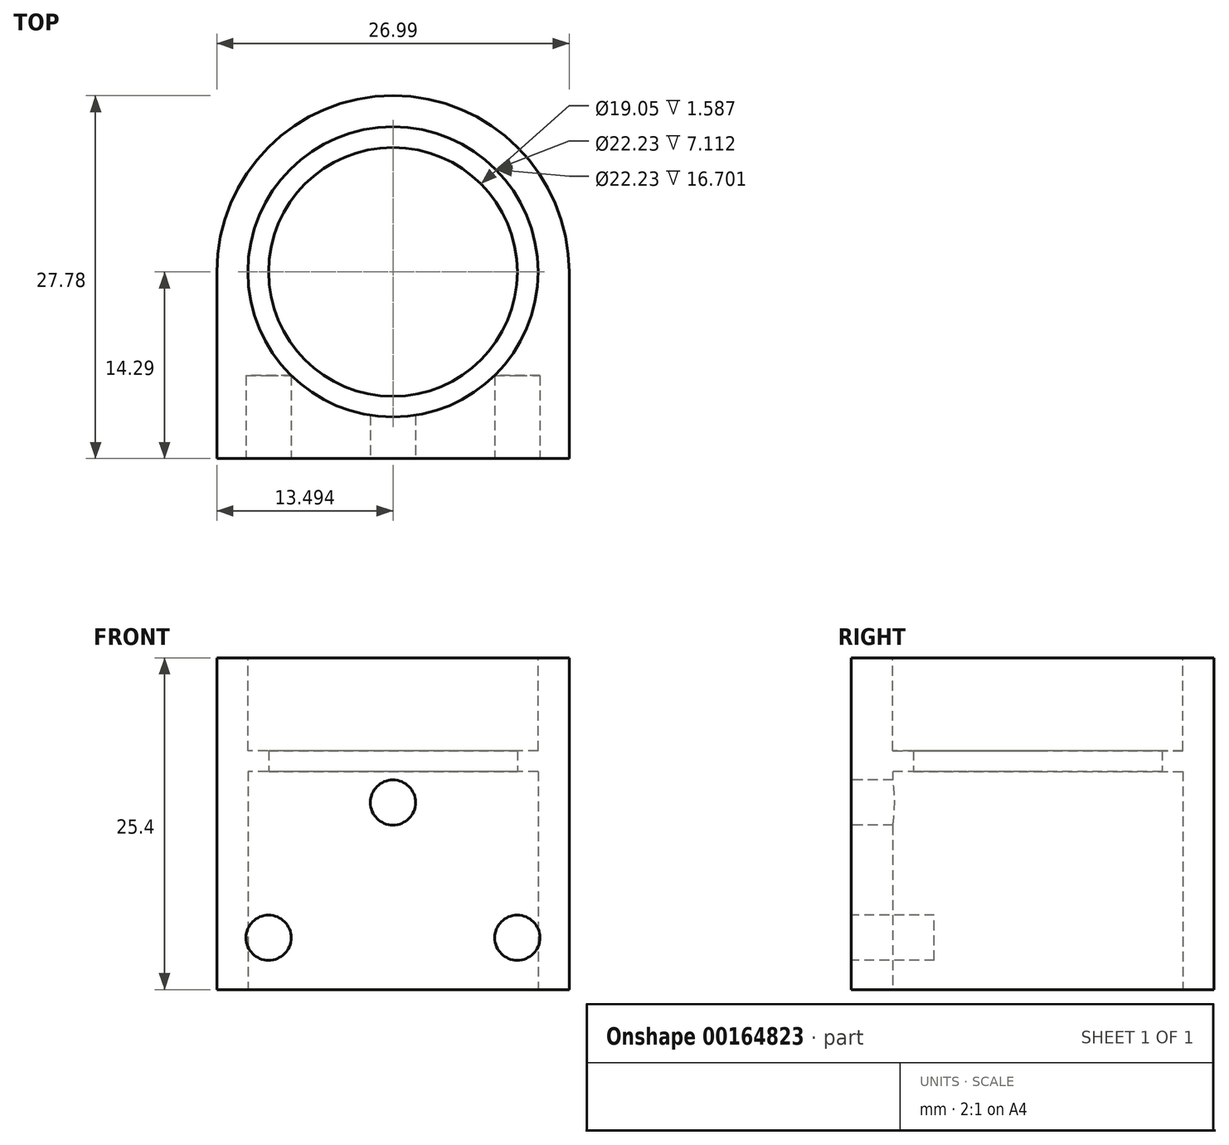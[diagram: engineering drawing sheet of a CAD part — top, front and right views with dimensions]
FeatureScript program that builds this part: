
annotation { "Feature Type Name" : "Feature", "Feature Type Description" : "" }
export const myFeature = defineFeature(function(context is Context, id is Id, definition is map)
    precondition{}
    {
        {
            var Q0;
            Q0=qCreatedBy(makeId("Top.planeOp"),FACE);
            var sketch = newSketch(context, id + "F0", { "sketchPlane" : qUnion([Q0])});
            skLineSegment(sketch, "E0.bottom", {"start": v(0, 0) * mm, "end": v(26.99, 0) * mm, "construction": true});
            skLineSegment(sketch, "E0.top", {"start": v(0, -14.29) * mm, "end": v(26.99, -14.29) * mm});
            skLineSegment(sketch, "E0.left", {"start": v(0, 0) * mm, "end": v(0, -14.29) * mm});
            skLineSegment(sketch, "E0.right", {"start": v(26.99, 0) * mm, "end": v(26.99, -14.29) * mm});
            skArc(sketch, "E1", {"start": v(26.99, 0) * mm, "mid": v(13.5, 13.5) * mm, "end": v(0, 0) * mm});
            skCircle(sketch, "E2", {"center": v(13.5, 0) * mm, "radius": 9.53 * mm});
            skArc(sketch, "E3", {"start": v(0, 0) * mm, "mid": v(13.5, -13.5) * mm, "end": v(26.99, 0) * mm, "construction": true});
            skLineSegment(sketch, "E4", {"start": v(23.02, -14.29) * mm, "end": v(23.02, -9.52) * mm, "construction": true});
            skLineSegment(sketch, "E5", {"start": v(19.05, -9.52) * mm, "end": v(26.99, -9.52) * mm, "construction": true});
            skSolve(sketch);
        }
        {
            var Q0;
            Q0 = qSketchRegion(id + "F0", true);
            extrude(context, id + "F1", {"entities" : qUnion([Q0]), "depth" : 25.4 * mm});
        }
        {
            var Q0;
            Q0=makeQuery(id+"F1.opExtrude","CAP_FACE",FACE,{"disambiguationData":[OSD([sQuery(id+"F0.wireOp",EDGE,"E0.top"),sQuery(id+"F0.wireOp",EDGE,"E0.left"),sQuery(id+"F0.wireOp",EDGE,"E0.right"),sQuery(id+"F0.wireOp",EDGE,"E1"),sQuery(id+"F0.wireOp",EDGE,"E2")])],"isStart":false});
            var sketch = newSketch(context, id + "F2", { "sketchPlane" : qUnion([Q0])});
            skCircle(sketch, "E6", {"center": v(13.5, 0) * mm, "radius": 11.11 * mm});
            skSolve(sketch);
        }
        {
            var Q0;
            Q0 = qSketchRegion(id + "F2", true);
            extrude(context, id + "F3", {"entities" : qUnion([Q0]), "operationType" : NewBodyOperationType.REMOVE, "oppositeDirection" : true, "depth" : 7.11 * mm});
        }
        {
            var Q0;
            Q0=makeQuery(id+"F3.boolean.opBoolean","COPY",FACE,{"derivedFrom":makeQuery(id+"F3.opExtrude","CAP_FACE",FACE,{"disambiguationData":[OSD([sQuery(id+"F2.wireOp",EDGE,"E6")])],"isStart":false})});
            cPlane(context, id + "F4", {"entities" : qUnion([Q0]), "cplaneType" : CPlaneType.OFFSET, "offset" : 1.59 * mm, "oppositeDirection" : true, "width" : 152.4 * mm, "height" : 152.4 * mm});
        }
        {
            var Q0;
            Q0=makeQuery(id+"F1.opExtrude","CAP_FACE",FACE,{"disambiguationData":[OSD([sQuery(id+"F0.wireOp",EDGE,"E0.top"),sQuery(id+"F0.wireOp",EDGE,"E0.left"),sQuery(id+"F0.wireOp",EDGE,"E0.right"),sQuery(id+"F0.wireOp",EDGE,"E1"),sQuery(id+"F0.wireOp",EDGE,"E2")])],"isStart":true});
            var sketch = newSketch(context, id + "F5", { "sketchPlane" : qUnion([Q0])});
            skCircle(sketch, "E7", {"center": v(13.5, 0) * mm, "radius": 11.11 * mm});
            skSolve(sketch);
        }
        {
            var Q0;
            Q0 = qSketchRegion(id + "F5", true);
            var Q1;
            Q1=qCreatedBy(id+"F4.planeOp",FACE);
            extrude(context, id + "F6", {"entities" : qUnion([Q0]), "operationType" : NewBodyOperationType.REMOVE, "endBound" : BoundingType.UP_TO_SURFACE, "oppositeDirection" : true, "endBoundEntityFace" : qUnion([Q1]), "depth" : 25.4 * mm});
        }
        {
            var Q0;
            Q0=makeQuery(id+"F1.opExtrude","SWEPT_FACE",FACE,{"disambiguationData":[OSD([sQuery(id+"F0.wireOp",EDGE,"E0.top")])]});
            var sketch = newSketch(context, id + "F7", { "sketchPlane" : qUnion([Q0])});
            skLineSegment(sketch, "E8.bottom", {"start": v(26.99, 0) * mm, "end": v(23.02, 0) * mm, "construction": true});
            skLineSegment(sketch, "E8.top", {"start": v(26.99, 3.97) * mm, "end": v(23.02, 3.97) * mm, "construction": true});
            skLineSegment(sketch, "E8.left", {"start": v(26.99, 0) * mm, "end": v(26.99, 3.97) * mm, "construction": true});
            skLineSegment(sketch, "E8.right", {"start": v(23.02, 0) * mm, "end": v(23.02, 3.97) * mm, "construction": true});
            skLineSegment(sketch, "E9.bottom", {"start": v(0, 0) * mm, "end": v(3.97, 0) * mm, "construction": true});
            skLineSegment(sketch, "E9.top", {"start": v(0, 3.97) * mm, "end": v(3.97, 3.97) * mm, "construction": true});
            skLineSegment(sketch, "E9.left", {"start": v(0, 0) * mm, "end": v(0, 3.97) * mm, "construction": true});
            skLineSegment(sketch, "E9.right", {"start": v(3.97, 0) * mm, "end": v(3.97, 3.97) * mm, "construction": true});
            skCircle(sketch, "E10", {"center": v(23.02, 3.97) * mm, "radius": 1.73 * mm});
            skCircle(sketch, "E11", {"center": v(3.97, 3.97) * mm, "radius": 1.73 * mm});
            skLineSegment(sketch, "E12", {"start": v(13.5, 18.29) * mm, "end": v(13.5, 14.32) * mm, "construction": true});
            skCircle(sketch, "E13", {"center": v(13.5, 14.32) * mm, "radius": 1.73 * mm});
            skSolve(sketch);
        }
        {
            var Q0;
            Q0=makeQuery(id+"F7.imprint","IMPRINT",FACE,{"disambiguationData":[TD([[makeQuery(id+"F7.imprint","IMPRINT",EDGE,{"derivedFrom":sQuery(id+"F7.wireOp",EDGE,"E10")}),1.0]])]});
            var Q1;
            Q1=makeQuery(id+"F7.imprint","IMPRINT",FACE,{"disambiguationData":[TD([[makeQuery(id+"F7.imprint","IMPRINT",EDGE,{"derivedFrom":sQuery(id+"F7.wireOp",EDGE,"E11")}),1.0]])]});
            var Q2;
            Q2=makeQuery(id+"F7.imprint","IMPRINT",FACE,{"disambiguationData":[TD([[makeQuery(id+"F7.imprint","IMPRINT",EDGE,{"derivedFrom":sQuery(id+"F7.wireOp",EDGE,"E13")}),1.0]])]});
            var Q3;
            Q3=makeQuery(id+"F6.boolean.opBoolean","COPY",FACE,{"derivedFrom":makeQuery(id+"F6.opExtrude","SWEPT_FACE",FACE,{"disambiguationData":[OSD([sQuery(id+"F5.wireOp",EDGE,"E7")])]})});
            extrude(context, id + "F8", {"entities" : qUnion([Q0, Q1, Q2]), "operationType" : NewBodyOperationType.REMOVE, "oppositeDirection" : true, "endBoundEntityFace" : qUnion([Q3]), "depth" : 6.35 * mm});
        }
    });
